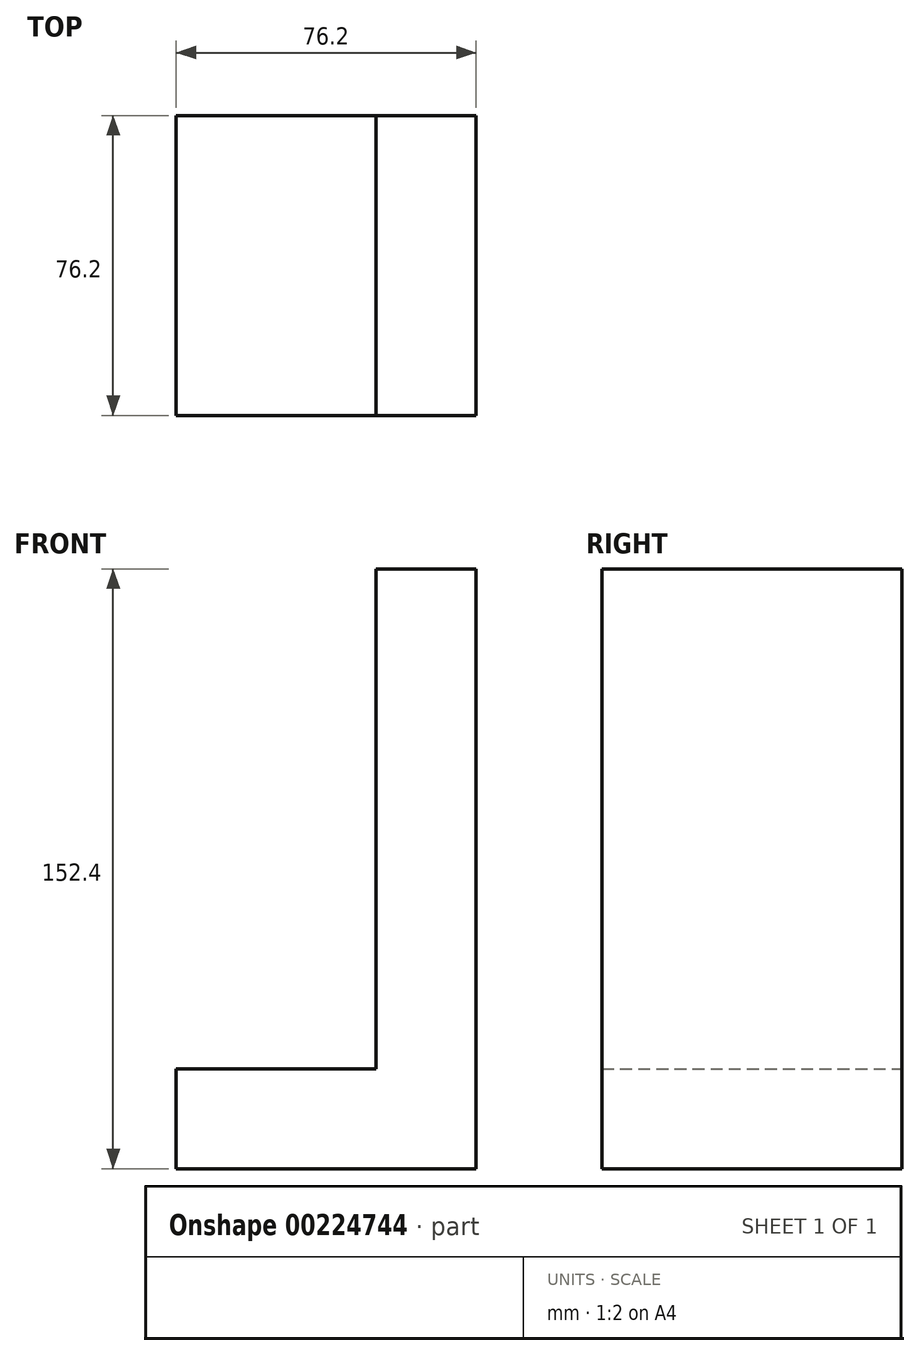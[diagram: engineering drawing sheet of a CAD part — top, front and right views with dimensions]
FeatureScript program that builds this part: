
annotation { "Feature Type Name" : "Feature", "Feature Type Description" : "" }
export const myFeature = defineFeature(function(context is Context, id is Id, definition is map)
    precondition{}
    {
        {
            var Q0;
            Q0=qCreatedBy(makeId("Front.planeOp"),FACE);
            var sketch = newSketch(context, id + "F0", { "sketchPlane" : qUnion([Q0])});
            skLineSegment(sketch, "E0", {"start": v(0, 152.4) * mm, "end": v(0, 0) * mm});
            skLineSegment(sketch, "E1", {"start": v(0, 0) * mm, "end": v(-76.2, 0) * mm});
            skLineSegment(sketch, "E2", {"start": v(-76.2, 0) * mm, "end": v(-76.2, 25.4) * mm});
            skLineSegment(sketch, "E3", {"start": v(-76.2, 25.4) * mm, "end": v(-25.4, 25.4) * mm});
            skLineSegment(sketch, "E4", {"start": v(-25.4, 25.4) * mm, "end": v(-25.4, 152.4) * mm});
            skLineSegment(sketch, "E5", {"start": v(-25.4, 152.4) * mm, "end": v(0, 152.4) * mm});
            skSolve(sketch);
        }
        {
            var Q0;
            Q0=makeQuery(id+"F0.imprint","IMPRINT",FACE,{"disambiguationData":[TD([[makeQuery(id+"F0.imprint","IMPRINT",EDGE,{"derivedFrom":sQuery(id+"F0.wireOp",EDGE,"E0")}),-1.0]])]});
            extrude(context, id + "F1", {"entities" : qUnion([Q0]), "depth" : 38.1 * mm, "hasSecondDirection" : true, "secondDirectionOppositeDirection" : true, "secondDirectionDepth" : 38.1 * mm});
        }
    });
